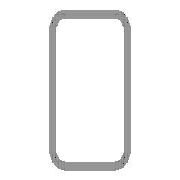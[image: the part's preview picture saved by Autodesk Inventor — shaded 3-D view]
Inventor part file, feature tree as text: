
AUTODESK INVENTOR PART (.ipt)
format: ipt  version: 2025 (Build 290162010, 162A)  size: 134,144 bytes
history: native  units: mm (DEFAULTED — no unit token found)
features: other x4, sketch x1, plane x1
ambient origin geometry x8: Origin, YZ Plane, XZ Plane, XY Plane, X Axis, Y Axis, Z Axis, Center Point
bodies: Solid1 (feature_tree), Body (feature_tree)
feature tree (6):
  parser-record x1  (decoder bookkeeping rows leaked as tree rows — omitted from the tree; the rows remain in map.json)
  other  "Driven Length"
  other  "Start Plane"
  other  "End Plane"
  sketch  "Sketch3"  dims[d3=1340.0mm d4=0.0mm d7=4.0mm d9=40.0mm d11=80.0mm d12=2.0mm d13=80.0mm d14=1420.0mm d15=20.0mm d16=40.0mm d17=90.0deg d18=1340.0mm]
  plane  "Work Plane3"
